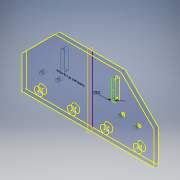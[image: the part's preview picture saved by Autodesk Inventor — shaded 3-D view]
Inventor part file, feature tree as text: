
AUTODESK INVENTOR PART (.ipt)
format: ipt  version: 2017 (Build 210142000, 142)  size: 193,024 bytes
history: native  units: in
note: dims shown in document units (in); Inventor stores cm internally (conversion verified against a paired STEP export)
features: sketch x5, projected_geometry x3, extrude x2, hole x2, mirror x2, pattern_linear x1, plane x1
ambient origin geometry x8: Origin, YZ Plane, XZ Plane, XY Plane, X Axis, Y Axis, Z Axis, Center Point
bodies: Solid1 (feature_tree)
feature tree (16):
  extrude  "Extrusion1"  Depth=2.0in
  hole  "Hole1"  [1 undecoded]
  pattern_linear  "Rectangular Pattern1"  Spacing1=4.0in  [1 undecoded]
  sketch  "Sketch3"  dims[d4=0.25in d5=0.0in]
  hole  "Hole2"  [1 undecoded]
  extrude  "Extrusion2"  Depth=2.0in
  sketch  "Sketch4"  dims[d6=0.5in]
  plane  "Work Plane1"
  mirror  "Mirror1"
  mirror  "Mirror2"
  sketch  "Sketch5"  dims[d7=8.0in d8=4.0in d9=1.0in d10=0.5in d11=0.75in d12=0.375in d13=0.25in d14=0.5635in d15=1.0in d16=0.8108in d17=1.5748in d19=2.0in d20=0.25in d21=0.196in d22=0.5in d23=0.119in d24=0.25in d25=0.5635in d26=0.75in d27=0.8108in d28=0.25in d29=0.0in d30=0.0in]
  sketch  "Sketch1"  dims[d0=2.0in d1=2.0in]
  sketch  "Sketch2"  dims[d2=2.0in d3=2.0in]
  projected_geometry  "Projected Loop1"
  projected_geometry  "Projected Loop2"
  projected_geometry  "Projected Loop3"
note: 3 required parameter values undecoded (feature->parameter linkage not recoverable at this tier; creation-order binding heuristic only, values carry confidence <= 0.55)
